# Revit family: BRG-GRF-CCN_CANBERRA MEZCLADOR DE DUCHA CROMO v_02
name_source: partatom
category: Aparatos sanitarios
units: mm (PartAtom-declared; Revit-internal decimal feet)

## family parameters
Anfitrión = Muro
Compartido = No
Corte con vacíos al cargar = No
Cota de conector redondo = Diámetro de uso
Número OmniClass = 23.45.00.00
Punto de cálculo de habitación = No
Siempre vertical = Sí
Tipo de pieza = Normal
Título OmniClass = Sanitary, Laundry, and Cleaning Equipment

## types (1)
- CANBERRA MEZCLADORA MONOMANDO DE DUCHA
    Fabricante = BRIGGS ECUADOR
    Modelo = CANBERRA MEZCLADORA MONOMANDO DE DUCHA
    URL = https://www.briggs.com.ec
    _ALT_ eje1 = 1.1 m
    _EDESA_ Alto en cm = 18
    _EDESA_ Ancho en cm = 13
    _EDESA_ Categoría = Productos > Grifería > Ducha
    _EDESA_ Certificación = Cumple con norma NTE - INEN 3123 basada en la norma ASME 112.18.1 - 2012.
    _EDESA_ Color = Cromo
    _EDESA_ Conexión hidráulica = Entrada de agua: tubería ø 1/2"
    _EDESA_ Consumo/capacidad de agua en L = 9.5 litros por minuto / 2.5 gpm en combinación con cualquiera de nuestras regaderas
    _EDESA_ Descripción = Grifería monomando de ducha para agua fría y caliente. Instalación empotrado en la pared.
    _EDESA_ Garantía = De por vida para el cuerpo principal y acabado en cromo (306)
    _EDESA_ Manual de instalación = https://www.briggs.com.ec
    _EDESA_ Marca = BRIGGS
    _EDESA_ Materiales = Latón
    _EDESA_ Nombre = CANBERRA MEZCLADORA MONOMANDO DE DUCHA
    _EDESA_ Productos necesarios para instalación = Regadera
    _EDESA_ Profundidad en cm = 6.7
    _EDESA_ Sku/código = SG0090013061CW
    _EDESA_ Tipo de instalación = Empotrado en la pared
